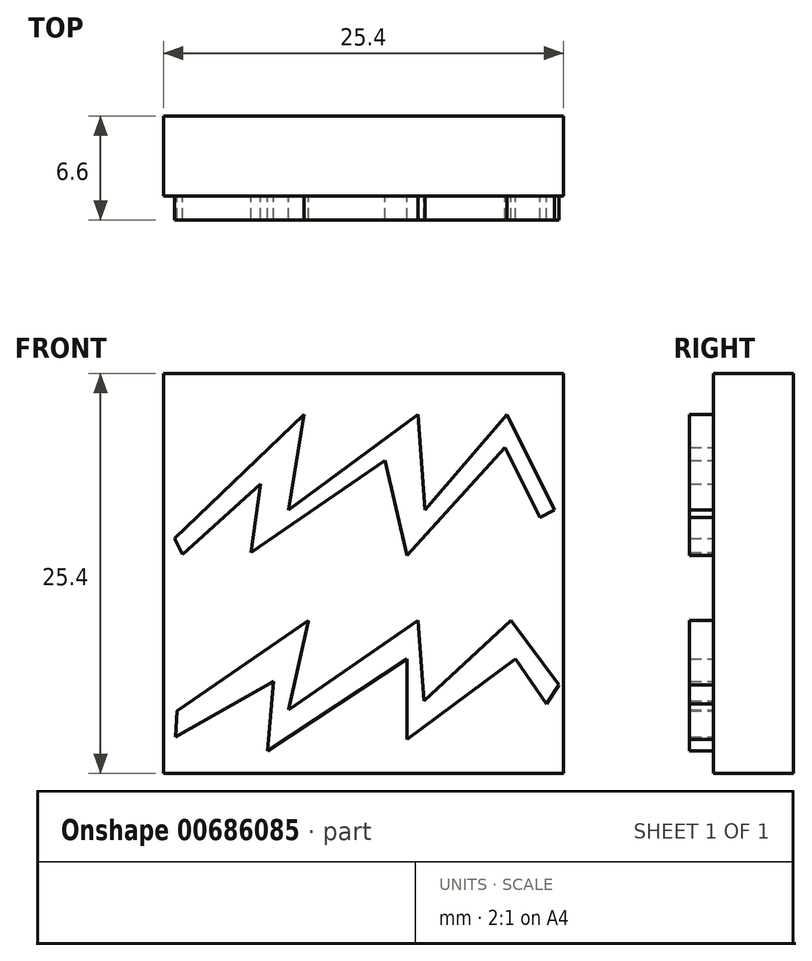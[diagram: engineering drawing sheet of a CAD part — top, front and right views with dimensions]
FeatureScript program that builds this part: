
annotation { "Feature Type Name" : "Feature", "Feature Type Description" : "" }
export const myFeature = defineFeature(function(context is Context, id is Id, definition is map)
    precondition{}
    {
        {
            var Q0;
            Q0=qCreatedBy(makeId("Front.planeOp"),FACE);
            var sketch = newSketch(context, id + "F0", { "sketchPlane" : qUnion([Q0])});
            skLineSegment(sketch, "E0.bottom", {"start": v(12.7, 12.7) * mm, "end": v(-12.7, 12.7) * mm});
            skLineSegment(sketch, "E0.top", {"start": v(12.7, -12.7) * mm, "end": v(-12.7, -12.7) * mm});
            skLineSegment(sketch, "E0.left", {"start": v(12.7, 12.7) * mm, "end": v(12.7, -12.7) * mm});
            skLineSegment(sketch, "E0.right", {"start": v(-12.7, 12.7) * mm, "end": v(-12.7, -12.7) * mm});
            skPoint(sketch, "E0.middle", {"position": v(0, 0) * mm});
            skSolve(sketch);
        }
        {
            var Q0;
            Q0 = qSketchRegion(id + "F0", true);
            extrude(context, id + "F1", {"entities" : qUnion([Q0]), "depth" : 5.08 * mm, "offsetDistance" : 25.4 * mm});
        }
        {
            var Q0;
            Q0=makeQuery(id+"F1.opExtrude","CAP_FACE",FACE,{"disambiguationData":[OSD([sQuery(id+"F0.wireOp",EDGE,"E0.bottom"),sQuery(id+"F0.wireOp",EDGE,"E0.top"),sQuery(id+"F0.wireOp",EDGE,"E0.left"),sQuery(id+"F0.wireOp",EDGE,"E0.right")])],"isStart":false});
            var sketch = newSketch(context, id + "F2", { "sketchPlane" : qUnion([Q0])});
            skLineSegment(sketch, "E1", {"start": v(-12, 2.2) * mm, "end": v(-3.77, 10.1) * mm});
            skLineSegment(sketch, "E2", {"start": v(-3.77, 10.1) * mm, "end": v(-4.76, 4.03) * mm});
            skLineSegment(sketch, "E3", {"start": v(-4.76, 4.03) * mm, "end": v(3.46, 10.1) * mm});
            skLineSegment(sketch, "E4", {"start": v(3.46, 10.1) * mm, "end": v(3.9, 4.03) * mm});
            skLineSegment(sketch, "E5", {"start": v(3.9, 4.03) * mm, "end": v(9.1, 10.1) * mm});
            skLineSegment(sketch, "E6", {"start": v(9.1, 10.1) * mm, "end": v(12.14, 4.03) * mm});
            skLineSegment(sketch, "E7", {"start": v(12.14, 4.03) * mm, "end": v(11.2, 3.57) * mm});
            skLineSegment(sketch, "E8", {"start": v(11.2, 3.57) * mm, "end": v(8.99, 8) * mm});
            skLineSegment(sketch, "E9", {"start": v(-12, 2.2) * mm, "end": v(-11.5, 1.21) * mm});
            skLineSegment(sketch, "E10", {"start": v(-11.5, 1.21) * mm, "end": v(-6.53, 5.7) * mm});
            skLineSegment(sketch, "E11", {"start": v(-6.53, 5.7) * mm, "end": v(-7.14, 1.32) * mm});
            skLineSegment(sketch, "E12", {"start": v(-7.14, 1.32) * mm, "end": v(1.36, 7.18) * mm});
            skLineSegment(sketch, "E13", {"start": v(1.36, 7.18) * mm, "end": v(2.75, 1.14) * mm});
            skLineSegment(sketch, "E14", {"start": v(2.75, 1.14) * mm, "end": v(8.99, 8) * mm});
            skLineSegment(sketch, "E15", {"start": v(-11.84, -8.72) * mm, "end": v(-3.5, -2.97) * mm});
            skLineSegment(sketch, "E16", {"start": v(-3.5, -2.97) * mm, "end": v(-4.76, -8.67) * mm});
            skLineSegment(sketch, "E17", {"start": v(-4.76, -8.67) * mm, "end": v(3.46, -2.97) * mm});
            skLineSegment(sketch, "E18", {"start": v(3.46, -2.97) * mm, "end": v(3.84, -8.08) * mm});
            skLineSegment(sketch, "E19", {"start": v(3.84, -8.08) * mm, "end": v(9.36, -2.97) * mm});
            skLineSegment(sketch, "E20", {"start": v(9.36, -2.97) * mm, "end": v(12.4, -7.08) * mm});
            skLineSegment(sketch, "E21", {"start": v(12.4, -7.08) * mm, "end": v(11.62, -8.28) * mm});
            skLineSegment(sketch, "E22", {"start": v(11.62, -8.28) * mm, "end": v(9.66, -5.44) * mm});
            skLineSegment(sketch, "E23", {"start": v(9.66, -5.44) * mm, "end": v(2.75, -10.55) * mm});
            skLineSegment(sketch, "E24", {"start": v(2.75, -10.55) * mm, "end": v(2.75, -5.44) * mm});
            skLineSegment(sketch, "E25", {"start": v(2.75, -5.44) * mm, "end": v(-6.1, -11.26) * mm});
            skLineSegment(sketch, "E26", {"start": v(-6.1, -11.26) * mm, "end": v(-5.71, -6.85) * mm});
            skLineSegment(sketch, "E27", {"start": v(-5.71, -6.85) * mm, "end": v(-11.95, -10.38) * mm});
            skLineSegment(sketch, "E28", {"start": v(-11.95, -10.38) * mm, "end": v(-11.84, -8.72) * mm});
            skSolve(sketch);
        }
        {
            var Q0;
            Q0 = qSketchRegion(id + "F2", true);
            extrude(context, id + "F3", {"entities" : qUnion([Q0]), "operationType" : NewBodyOperationType.ADD, "depth" : 1.52 * mm, "offsetDistance" : 25.4 * mm});
        }
    });
